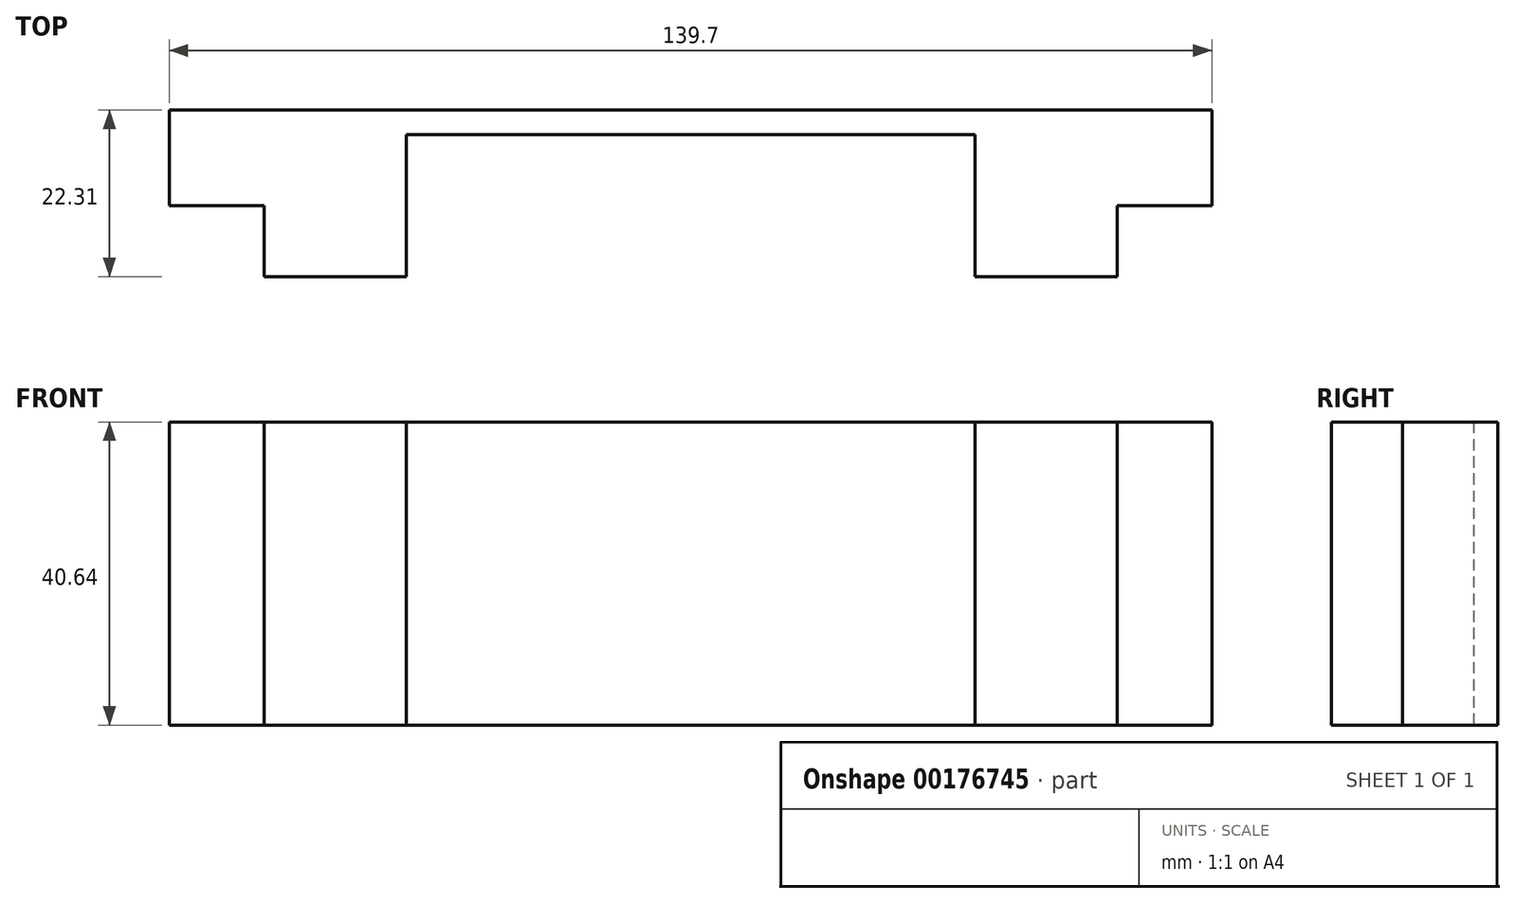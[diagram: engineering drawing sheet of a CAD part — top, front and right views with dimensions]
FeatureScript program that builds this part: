
annotation { "Feature Type Name" : "Feature", "Feature Type Description" : "" }
export const myFeature = defineFeature(function(context is Context, id is Id, definition is map)
    precondition{}
    {
        {
            var Q0;
            Q0=qCreatedBy(makeId("Top.planeOp"),FACE);
            var sketch = newSketch(context, id + "F0", { "sketchPlane" : qUnion([Q0])});
            skLineSegment(sketch, "E0", {"start": v(-62.11, 12.78) * mm, "end": v(77.59, 12.78) * mm});
            skLineSegment(sketch, "E1", {"start": v(-62.11, 12.78) * mm, "end": v(-62.11, 0) * mm});
            skLineSegment(sketch, "E2", {"start": v(77.59, 12.78) * mm, "end": v(77.59, 0) * mm});
            skLineSegment(sketch, "E3", {"start": v(77.59, 0) * mm, "end": v(64.89, 0) * mm});
            skLineSegment(sketch, "E4", {"start": v(-62.11, 0) * mm, "end": v(-49.41, 0) * mm});
            skLineSegment(sketch, "E5", {"start": v(-49.41, 0) * mm, "end": v(-49.41, -9.53) * mm});
            skLineSegment(sketch, "E6", {"start": v(64.89, 0) * mm, "end": v(64.89, -9.52) * mm});
            skLineSegment(sketch, "E7", {"start": v(-49.41, -9.53) * mm, "end": v(-30.36, -9.53) * mm});
            skLineSegment(sketch, "E8", {"start": v(64.89, -9.52) * mm, "end": v(45.84, -9.52) * mm});
            skLineSegment(sketch, "E9", {"start": v(-30.36, -9.53) * mm, "end": v(-30.36, 9.53) * mm});
            skLineSegment(sketch, "E10", {"start": v(45.84, -9.52) * mm, "end": v(45.84, 9.53) * mm});
            skLineSegment(sketch, "E11", {"start": v(-30.36, 9.52) * mm, "end": v(45.84, 9.53) * mm});
            skSolve(sketch);
        }
        {
            var Q0;
            Q0=makeQuery(id+"F0.imprint","IMPRINT",FACE,{"disambiguationData":[TD([[makeQuery(id+"F0.imprint","IMPRINT",EDGE,{"derivedFrom":sQuery(id+"F0.wireOp",EDGE,"E0")}),-1.0]])]});
            extrude(context, id + "F1", {"entities" : qUnion([Q0]), "depth" : 40.64 * mm});
        }
    });
